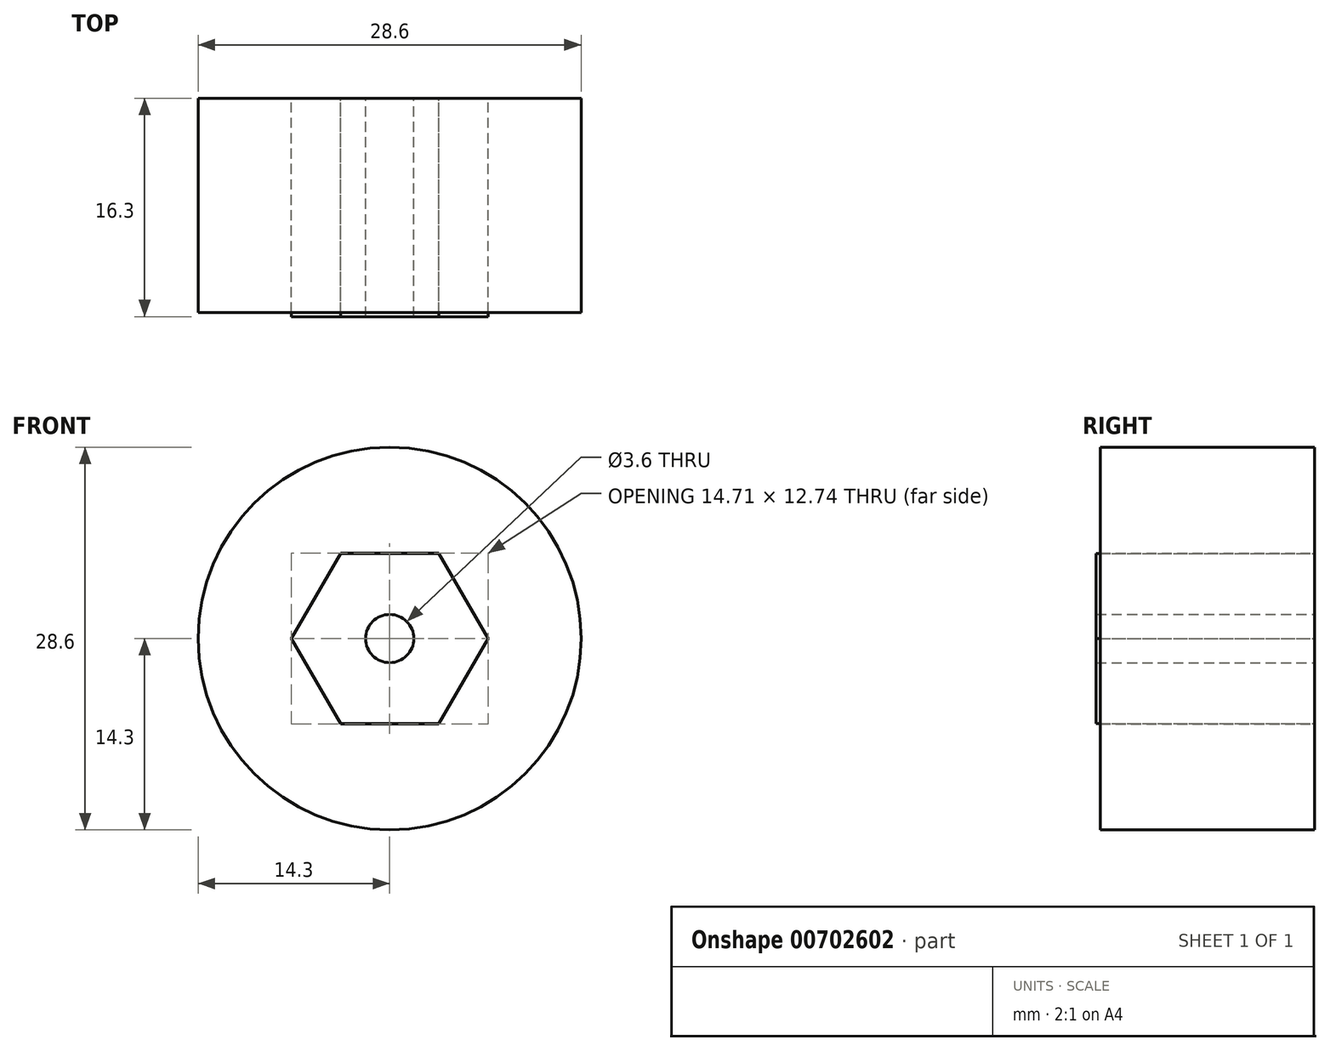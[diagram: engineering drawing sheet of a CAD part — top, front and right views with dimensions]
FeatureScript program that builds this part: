
annotation { "Feature Type Name" : "Feature", "Feature Type Description" : "" }
export const myFeature = defineFeature(function(context is Context, id is Id, definition is map)
    precondition{}
    {
        {
            var Q0;
            Q0=qCreatedBy(makeId("Front.planeOp"),FACE);
            var sketch = newSketch(context, id + "F0", { "sketchPlane" : qUnion([Q0])});
            skCircle(sketch, "E0.cCircle", {"center": v(0, 0) * mm, "radius": 6.37 * mm, "construction": true});
            skLineSegment(sketch, "E0.0", {"start": v(-3.67, 6.37) * mm, "end": v(3.67, 6.37) * mm});
            skLineSegment(sketch, "E0.1", {"start": v(3.67, 6.37) * mm, "end": v(7.35, 0) * mm});
            skLineSegment(sketch, "E0.2", {"start": v(7.35, 0) * mm, "end": v(3.67, -6.36) * mm});
            skLineSegment(sketch, "E0.3", {"start": v(3.67, -6.36) * mm, "end": v(-3.67, -6.37) * mm});
            skLineSegment(sketch, "E0.4", {"start": v(-3.67, -6.36) * mm, "end": v(-7.35, 0) * mm});
            skLineSegment(sketch, "E0.5", {"start": v(-7.35, 0) * mm, "end": v(-3.67, 6.36) * mm});
            skPoint(sketch, "E0.0.midPoint", {"position": v(0, 6.37) * mm});
            skCircle(sketch, "E1", {"center": v(0, 0) * mm, "radius": 1.8 * mm});
            skSolve(sketch);
        }
        {
            var Q0;
            Q0 = qSketchRegion(id + "F0", true);
            extrude(context, id + "F1", {"entities" : qUnion([Q0]), "depth" : 16.3 * mm, "offsetDistance" : 25 * mm});
        }
        {
            var Q0;
            Q0=qCreatedBy(makeId("Front.planeOp"),FACE);
            var sketch = newSketch(context, id + "F2", { "sketchPlane" : qUnion([Q0])});
            skCircle(sketch, "E2", {"center": v(0, 0) * mm, "radius": 14.3 * mm});
            skCircle(sketch, "E3.cCircle", {"center": v(0, 0) * mm, "radius": 6.37 * mm, "construction": true});
            skLineSegment(sketch, "E3.0", {"start": v(-3.68, 6.37) * mm, "end": v(3.68, 6.37) * mm});
            skLineSegment(sketch, "E3.1", {"start": v(3.68, 6.37) * mm, "end": v(7.36, 0) * mm});
            skLineSegment(sketch, "E3.2", {"start": v(7.36, 0) * mm, "end": v(3.68, -6.37) * mm});
            skLineSegment(sketch, "E3.3", {"start": v(3.68, -6.37) * mm, "end": v(-3.68, -6.37) * mm});
            skLineSegment(sketch, "E3.4", {"start": v(-3.68, -6.37) * mm, "end": v(-7.36, 0) * mm});
            skLineSegment(sketch, "E3.5", {"start": v(-7.36, 0) * mm, "end": v(-3.68, 6.37) * mm});
            skPoint(sketch, "E3.0.midPoint", {"position": v(0, 6.37) * mm});
            skCircle(sketch, "E4", {"center": v(0, 0) * mm, "radius": 1.5 * mm});
            skSolve(sketch);
        }
        {
            var Q0;
            Q0 = qSketchRegion(id + "F2", true);
            extrude(context, id + "F3", {"entities" : qUnion([Q0]), "depth" : 16 * mm, "offsetDistance" : 25 * mm});
        }
    });
